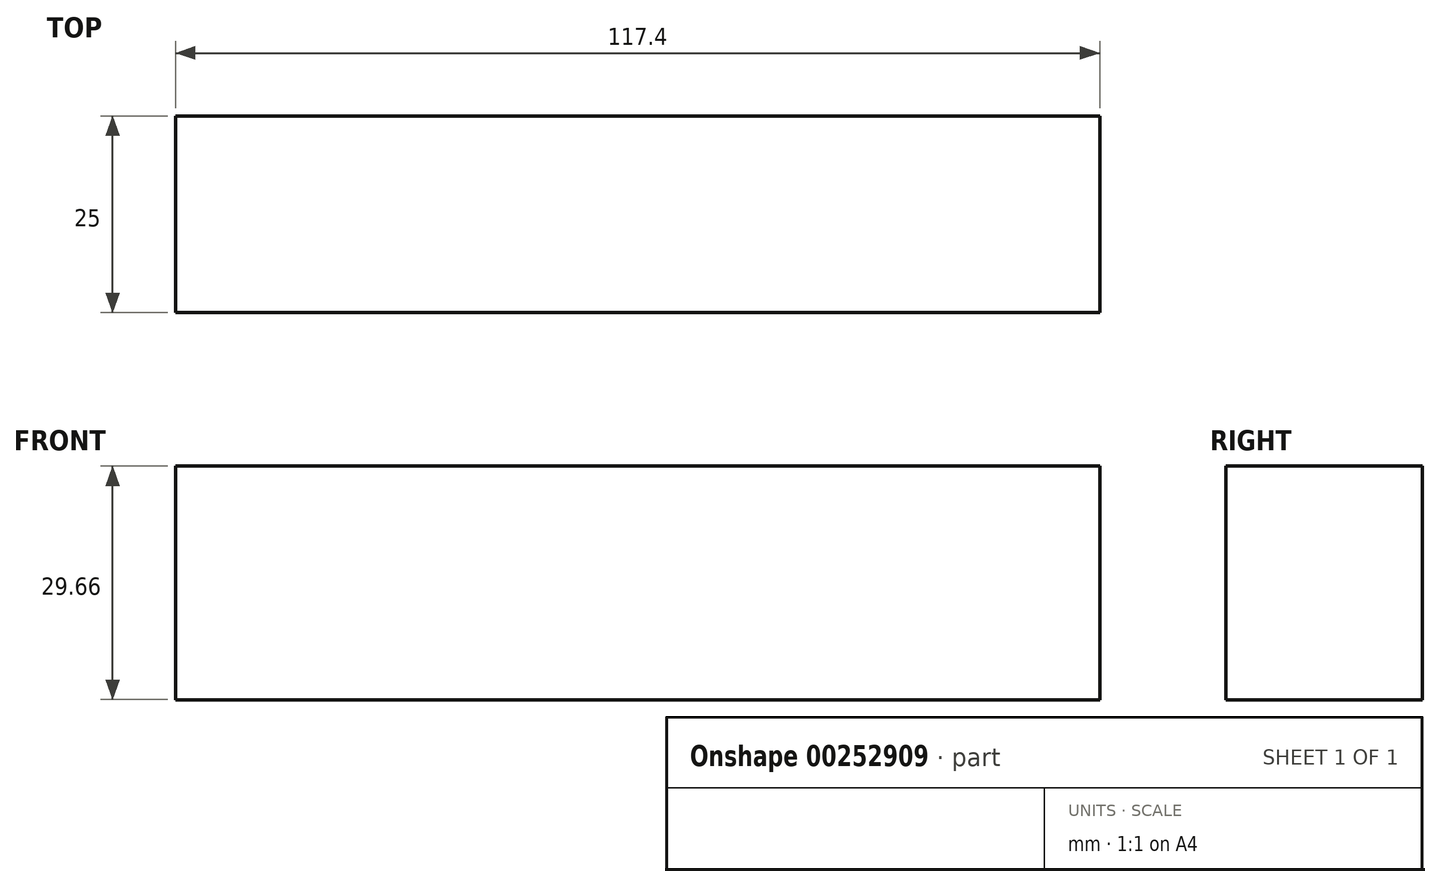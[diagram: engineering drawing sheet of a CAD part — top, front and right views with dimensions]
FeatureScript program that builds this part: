
annotation { "Feature Type Name" : "Feature", "Feature Type Description" : "" }
export const myFeature = defineFeature(function(context is Context, id is Id, definition is map)
    precondition{}
    {
        {
            var Q0;
            Q0=qCreatedBy(makeId("Front.planeOp"),FACE);
            var sketch = newSketch(context, id + "F0", { "sketchPlane" : qUnion([Q0])});
            skLineSegment(sketch, "E0.bottom", {"start": v(58.7, -14.83) * mm, "end": v(-58.7, -14.83) * mm});
            skLineSegment(sketch, "E0.top", {"start": v(58.7, 14.83) * mm, "end": v(-58.7, 14.83) * mm});
            skLineSegment(sketch, "E0.left", {"start": v(58.7, -14.83) * mm, "end": v(58.7, 14.83) * mm});
            skLineSegment(sketch, "E0.right", {"start": v(-58.7, -14.83) * mm, "end": v(-58.7, 14.83) * mm});
            skPoint(sketch, "E0.middle", {"position": v(0, 0) * mm});
            skSolve(sketch);
        }
        {
            var Q0;
            Q0=makeQuery(id+"F0.imprint","IMPRINT",FACE,{"disambiguationData":[TD([[makeQuery(id+"F0.imprint","IMPRINT",EDGE,{"derivedFrom":sQuery(id+"F0.wireOp",EDGE,"E0.bottom")}),-1.0]])]});
            extrude(context, id + "F1", {"entities" : qUnion([Q0]), "depth" : 25 * mm});
        }
    });
